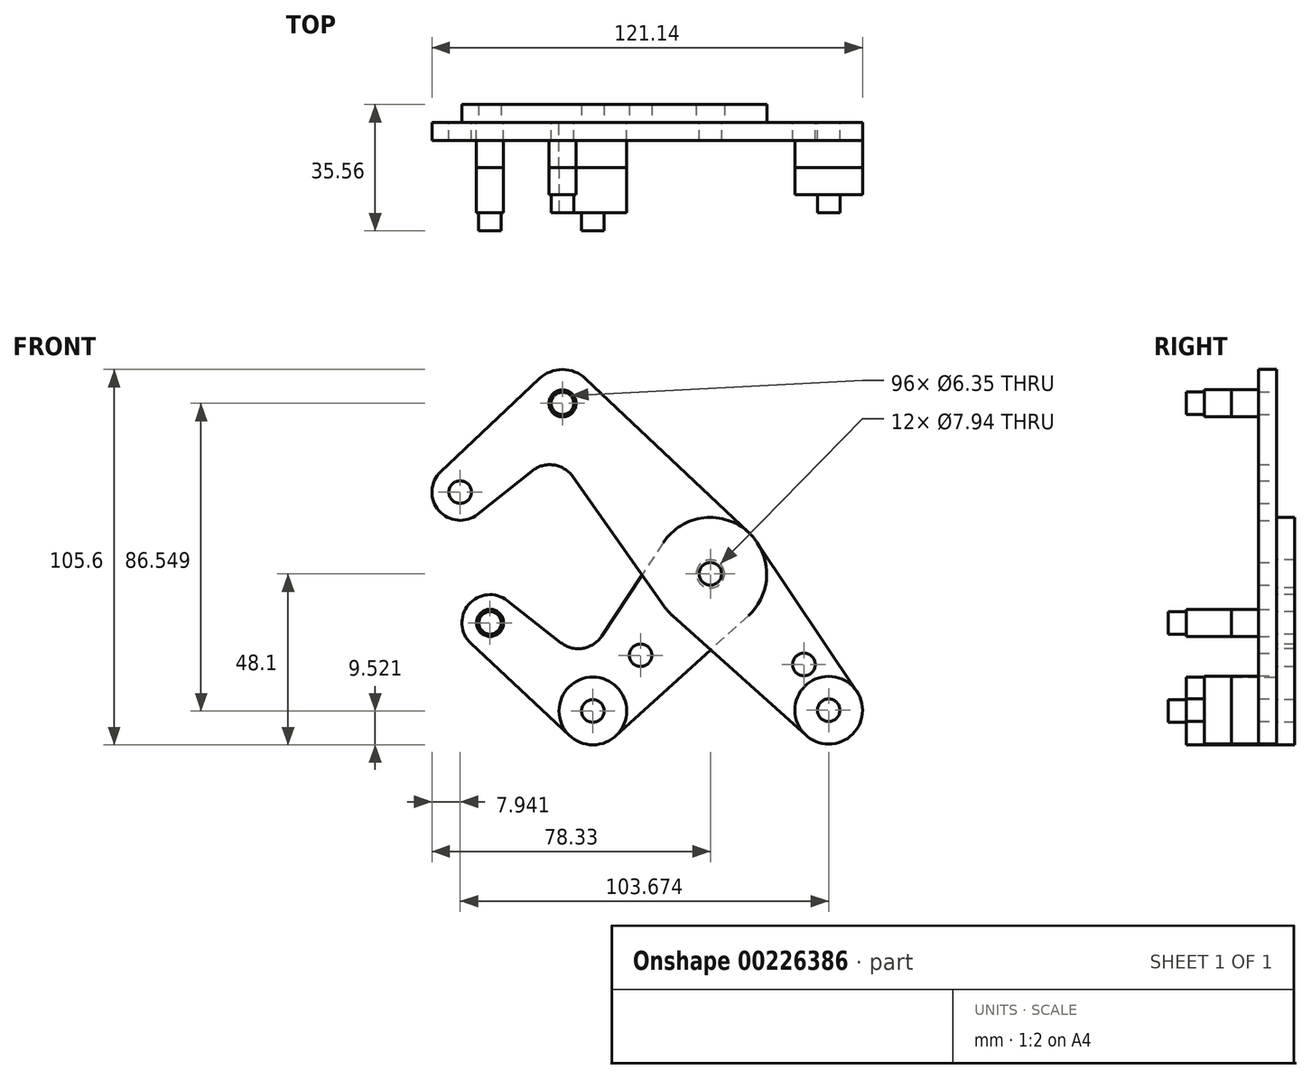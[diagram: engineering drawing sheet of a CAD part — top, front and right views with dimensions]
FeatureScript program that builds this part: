
annotation { "Feature Type Name" : "Feature", "Feature Type Description" : "" }
export const myFeature = defineFeature(function(context is Context, id is Id, definition is map)
    precondition{}
    {
        {
            var Q0;
            Q0=qCreatedBy(makeId("Front.planeOp"),FACE);
            var sketch = newSketch(context, id + "F0", { "sketchPlane" : qUnion([Q0])});
            skLineSegment(sketch, "E0", {"start": v(-41.6, 47.97) * mm, "end": v(41.6, -47.97) * mm, "construction": true});
            skCircle(sketch, "E1", {"center": v(0, 0) * mm, "radius": 3.18 * mm});
            skCircle(sketch, "E2", {"center": v(33.29, -38.38) * mm, "radius": 3.18 * mm});
            skCircle(sketch, "E3", {"center": v(-41.6, 47.97) * mm, "radius": 3.18 * mm});
            skCircle(sketch, "E4", {"center": v(-70.39, 23) * mm, "radius": 3.18 * mm});
            skLineSegment(sketch, "E5", {"start": v(-41.6, 47.97) * mm, "end": v(-70.39, 23) * mm, "construction": true});
            skCircle(sketch, "E6", {"center": v(33.29, -38.38) * mm, "radius": 9.53 * mm});
            skCircle(sketch, "E7", {"center": v(-70.39, 23) * mm, "radius": 7.94 * mm});
            skCircle(sketch, "E8", {"center": v(-41.6, 47.97) * mm, "radius": 9.53 * mm});
            skLineSegment(sketch, "E9", {"start": v(-75.83, 28.78) * mm, "end": v(-48.14, 54.9) * mm});
            skLineSegment(sketch, "E10", {"start": v(-65.44, 16.8) * mm, "end": v(-50.15, 28.98) * mm});
            skCircle(sketch, "E11", {"center": v(0, 0) * mm, "radius": 15.88 * mm});
            skLineSegment(sketch, "E12", {"start": v(-35.07, 54.9) * mm, "end": v(10.9, 11.55) * mm});
            skLineSegment(sketch, "E13", {"start": v(-38.72, 27.35) * mm, "end": v(-12.97, -9.15) * mm});
            skLineSegment(sketch, "E14", {"start": v(-10.6, -11.82) * mm, "end": v(26.93, -45.47) * mm});
            skLineSegment(sketch, "E15", {"start": v(13.2, 8.82) * mm, "end": v(41.2, -33.08) * mm});
            skArc(sketch, "E16.filletArc", {"start": v(-38.72, 27.35) * mm, "mid": v(-44.08, 30.63) * mm, "end": v(-50.15, 28.98) * mm});
            skLineSegment(sketch, "E17", {"start": v(0, 0) * mm, "end": v(-33.05, -38.58) * mm, "construction": true});
            skLineSegment(sketch, "E18", {"start": v(-33.05, -38.58) * mm, "end": v(-61.98, -13.8) * mm, "construction": true});
            skCircle(sketch, "E19", {"center": v(-61.98, -13.8) * mm, "radius": 3.18 * mm});
            skCircle(sketch, "E20", {"center": v(-33.05, -38.58) * mm, "radius": 3.18 * mm});
            skCircle(sketch, "E21", {"center": v(-61.98, -13.8) * mm, "radius": 7.94 * mm});
            skCircle(sketch, "E22", {"center": v(-33.05, -38.58) * mm, "radius": 9.53 * mm});
            skLineSegment(sketch, "E23", {"start": v(-57.08, -7.55) * mm, "end": v(-42.08, -19.35) * mm});
            skLineSegment(sketch, "E24", {"start": v(-67.4, -19.6) * mm, "end": v(-39.54, -45.55) * mm});
            skLineSegment(sketch, "E25", {"start": v(-13.25, 8.74) * mm, "end": v(-30.55, -17.48) * mm});
            skLineSegment(sketch, "E26", {"start": v(10.67, -11.75) * mm, "end": v(-26.65, -45.63) * mm});
            skArc(sketch, "E27.filletArc", {"start": v(-42.08, -19.35) * mm, "mid": v(-35.9, -20.95) * mm, "end": v(-30.55, -17.48) * mm});
            skCircle(sketch, "E28", {"center": v(-19.62, -22.9) * mm, "radius": 3.18 * mm});
            skCircle(sketch, "E29", {"center": v(26.32, -25.5) * mm, "radius": 3.18 * mm});
            skLineSegment(sketch, "E30", {"start": v(26.32, -25.5) * mm, "end": v(23.92, -27.58) * mm, "construction": true});
            skCircle(sketch, "E31", {"center": v(0, 0) * mm, "radius": 3.97 * mm});
            skSolve(sketch);
        }
        {
            var Q0;
            Q0=qCreatedBy(makeId("Front.planeOp"),FACE);
            cPlane(context, id + "F1", {"entities" : qUnion([Q0]), "cplaneType" : CPlaneType.OFFSET, "offset" : 12.7 * mm, "width" : 254 * mm, "height" : 254 * mm});
        }
        {
            var Q0;
            Q0=makeQuery(id+"F0.imprint","IMPRINT",FACE,{"disambiguationData":[TD([[makeQuery(id+"F0.imprint","IMPRINT",EDGE,{"derivedFrom":sQuery(id+"F0.wireOp",EDGE,"E4")}),-1.0]])]});
            var Q1;
            {var subQ1=sQuery(id+"F0.wireOp",EDGE,"E9");Q1=makeQuery(id+"F0.imprint","IMPRINT",FACE,{"disambiguationData":[TD([[makeQuery(id+"F0.imprint","IMPRINT",EDGE,{"derivedFrom":subQ1}),-1.0]])]});}
            var Q2;
            Q2=makeQuery(id+"F0.imprint","IMPRINT",FACE,{"disambiguationData":[TD([[makeQuery(id+"F0.imprint","IMPRINT",EDGE,{"derivedFrom":sQuery(id+"F0.wireOp",EDGE,"E3")}),-1.0]])]});
            var Q3;
            Q3=makeQuery(id+"F0.imprint","IMPRINT",FACE,{"disambiguationData":[TD([[makeQuery(id+"F0.imprint","IMPRINT",EDGE,{"derivedFrom":sQuery(id+"F0.wireOp",EDGE,"E31")}),-1.0]])]});
            var Q4;
            {var subQ0=sQuery(id+"F0.wireOp",EDGE,"E13");var subQ1=sQuery(id+"F0.wireOp",EDGE,"E11");var subQ2=makeQuery(id+"F0.imprint","INTERSECT",VERTEX,{"derivedFrom":[subQ1,subQ0]});Q4=makeQuery(id+"F0.imprint","IMPRINT",FACE,{"disambiguationData":[TD([[makeQuery(id+"F0.imprint","IMPRINT",EDGE,{"disambiguationData":[TD([[subQ2,1.0]])],"derivedFrom":subQ1}),-1.0]])]});}
            var Q5;
            {var subQ0=sQuery(id+"F0.wireOp",EDGE,"E14");var subQ1=sQuery(id+"F0.wireOp",EDGE,"E11");var subQ2=makeQuery(id+"F0.imprint","INTERSECT",VERTEX,{"derivedFrom":[subQ1,subQ0]});Q5=makeQuery(id+"F0.imprint","IMPRINT",FACE,{"disambiguationData":[TD([[makeQuery(id+"F0.imprint","IMPRINT",EDGE,{"disambiguationData":[TD([[subQ2,-1.0]])],"derivedFrom":subQ1}),-1.0]])]});}
            var Q6;
            {var subQ0=sQuery(id+"F0.wireOp",EDGE,"E15");Q6=makeQuery(id+"F0.imprint","IMPRINT",FACE,{"disambiguationData":[TD([[makeQuery(id+"F0.imprint","IMPRINT",EDGE,{"derivedFrom":subQ0}),-1.0]])]});}
            var Q7;
            Q7=makeQuery(id+"F0.imprint","IMPRINT",FACE,{"disambiguationData":[TD([[makeQuery(id+"F0.imprint","IMPRINT",EDGE,{"derivedFrom":sQuery(id+"F0.wireOp",EDGE,"E2")}),-1.0]])]});
            var Q8;
            Q8=makeQuery(id+"F0.imprint","IMPRINT",FACE,{"disambiguationData":[TD([[makeQuery(id+"F0.imprint","IMPRINT",EDGE,{"derivedFrom":sQuery(id+"F0.wireOp",EDGE,"E1")}),-1.0]])]});
            extrude(context, id + "F2", {"entities" : qUnion([Q0, Q1, Q2, Q3, Q4, Q5, Q6, Q7, Q8]), "depth" : 5.08 * mm});
        }
        {
            var Q0;
            Q0=makeQuery(id+"F0.imprint","IMPRINT",FACE,{"disambiguationData":[TD([[makeQuery(id+"F0.imprint","IMPRINT",EDGE,{"derivedFrom":sQuery(id+"F0.wireOp",EDGE,"E31")}),-1.0]])]});
            var Q1;
            {var subQ0=sQuery(id+"F0.wireOp",EDGE,"E14");var subQ1=sQuery(id+"F0.wireOp",EDGE,"E11");var subQ2=makeQuery(id+"F0.imprint","INTERSECT",VERTEX,{"derivedFrom":[subQ1,subQ0]});Q1=makeQuery(id+"F0.imprint","IMPRINT",FACE,{"disambiguationData":[TD([[makeQuery(id+"F0.imprint","IMPRINT",EDGE,{"disambiguationData":[TD([[subQ2,-1.0]])],"derivedFrom":subQ1}),-1.0]])]});}
            var Q2;
            {var subQ10=sQuery(id+"F0.wireOp",EDGE,"E23");Q2=makeQuery(id+"F0.imprint","IMPRINT",FACE,{"disambiguationData":[TD([[makeQuery(id+"F0.imprint","IMPRINT",EDGE,{"derivedFrom":subQ10}),-1.0]])]});}
            var Q3;
            {var subQ0=sQuery(id+"F0.wireOp",EDGE,"E13");var subQ1=sQuery(id+"F0.wireOp",EDGE,"E11");var subQ2=makeQuery(id+"F0.imprint","INTERSECT",VERTEX,{"derivedFrom":[subQ1,subQ0]});Q3=makeQuery(id+"F0.imprint","IMPRINT",FACE,{"disambiguationData":[TD([[makeQuery(id+"F0.imprint","IMPRINT",EDGE,{"disambiguationData":[TD([[subQ2,1.0]])],"derivedFrom":subQ1}),-1.0]])]});}
            var Q4;
            Q4=makeQuery(id+"F0.imprint","IMPRINT",FACE,{"disambiguationData":[TD([[makeQuery(id+"F0.imprint","IMPRINT",EDGE,{"derivedFrom":sQuery(id+"F0.wireOp",EDGE,"E19")}),-1.0]])]});
            var Q5;
            Q5=makeQuery(id+"F0.imprint","IMPRINT",FACE,{"disambiguationData":[TD([[makeQuery(id+"F0.imprint","IMPRINT",EDGE,{"derivedFrom":sQuery(id+"F0.wireOp",EDGE,"E20")}),-1.0]])]});
            extrude(context, id + "F3", {"entities" : qUnion([Q0, Q1, Q2, Q3, Q4, Q5]), "oppositeDirection" : true, "depth" : 5.08 * mm});
        }
        {
            var Q0;
            Q0=makeQuery(id+"F2.opExtrude","CAP_FACE",FACE,{"disambiguationData":[OSD([sQuery(id+"F0.wireOp",EDGE,"E1"),sQuery(id+"F0.wireOp",EDGE,"E2"),sQuery(id+"F0.wireOp",EDGE,"E3"),sQuery(id+"F0.wireOp",EDGE,"E4"),sQuery(id+"F0.wireOp",EDGE,"E6"),sQuery(id+"F0.wireOp",EDGE,"E7"),sQuery(id+"F0.wireOp",EDGE,"E8"),sQuery(id+"F0.wireOp",EDGE,"E9"),sQuery(id+"F0.wireOp",EDGE,"E10"),sQuery(id+"F0.wireOp",EDGE,"E11"),sQuery(id+"F0.wireOp",EDGE,"E12"),sQuery(id+"F0.wireOp",EDGE,"E13"),sQuery(id+"F0.wireOp",EDGE,"E14"),sQuery(id+"F0.wireOp",EDGE,"E15"),sQuery(id+"F0.wireOp",EDGE,"E16.filletArc"),sQuery(id+"F0.wireOp",EDGE,"E29")])],"isStart":true});
            var sketch = newSketch(context, id + "F4", { "sketchPlane" : qUnion([Q0])});
            skCircle(sketch, "E32", {"center": v(41.6, 47.97) * mm, "radius": 3.81 * mm});
            skCircle(sketch, "E33.0", {"center": v(-33.29, -38.38) * mm, "radius": 9.53 * mm});
            skSolve(sketch);
        }
        {
            var Q0;
            Q0=makeQuery(id+"F3.opExtrude","CAP_FACE",FACE,{"disambiguationData":[OSD([sQuery(id+"F0.wireOp",EDGE,"E11"),sQuery(id+"F0.wireOp",EDGE,"E19"),sQuery(id+"F0.wireOp",EDGE,"E20"),sQuery(id+"F0.wireOp",EDGE,"E21"),sQuery(id+"F0.wireOp",EDGE,"E22"),sQuery(id+"F0.wireOp",EDGE,"E23"),sQuery(id+"F0.wireOp",EDGE,"E24"),sQuery(id+"F0.wireOp",EDGE,"E25"),sQuery(id+"F0.wireOp",EDGE,"E26"),sQuery(id+"F0.wireOp",EDGE,"E27.filletArc"),sQuery(id+"F0.wireOp",EDGE,"E28"),sQuery(id+"F0.wireOp",EDGE,"E31")])],"isStart":false});
            var sketch = newSketch(context, id + "F5", { "sketchPlane" : qUnion([Q0])});
            skCircle(sketch, "E34", {"center": v(61.98, -13.8) * mm, "radius": 3.81 * mm});
            skCircle(sketch, "E35.0", {"center": v(33.05, -38.58) * mm, "radius": 9.53 * mm});
            skSolve(sketch);
        }
        {
            var Q0;
            Q0=qSketchRegion(id+"F4",true);
            var Q1;
            Q1=qSketchRegion(id+"F5",true);
            var Q2;
            Q2=qCreatedBy(id+"F1.planeOp",FACE);
            extrude(context, id + "F6", {"entities" : qUnion([Q0, Q1]), "endBound" : BoundingType.UP_TO_SURFACE, "oppositeDirection" : true, "endBoundEntityFace" : qUnion([Q2]), "depth" : 25.4 * mm});
        }
        {
            var Q0;
            Q0=makeQuery(id+"F2.opExtrude","SWEPT_BODY",BODY,{"disambiguationData":[OSD([sQuery(id+"F0.wireOp",EDGE,"E1"),sQuery(id+"F0.wireOp",EDGE,"E2"),sQuery(id+"F0.wireOp",EDGE,"E3"),sQuery(id+"F0.wireOp",EDGE,"E4"),sQuery(id+"F0.wireOp",EDGE,"E6"),sQuery(id+"F0.wireOp",EDGE,"E7"),sQuery(id+"F0.wireOp",EDGE,"E8"),sQuery(id+"F0.wireOp",EDGE,"E9"),sQuery(id+"F0.wireOp",EDGE,"E10"),sQuery(id+"F0.wireOp",EDGE,"E11"),sQuery(id+"F0.wireOp",EDGE,"E12"),sQuery(id+"F0.wireOp",EDGE,"E13"),sQuery(id+"F0.wireOp",EDGE,"E14"),sQuery(id+"F0.wireOp",EDGE,"E15"),sQuery(id+"F0.wireOp",EDGE,"E16.filletArc"),sQuery(id+"F0.wireOp",EDGE,"E29")])]});
            var Q1;
            Q1=makeQuery(id+"F3.opExtrude","SWEPT_BODY",BODY,{"disambiguationData":[OSD([sQuery(id+"F0.wireOp",EDGE,"E11"),sQuery(id+"F0.wireOp",EDGE,"E19"),sQuery(id+"F0.wireOp",EDGE,"E20"),sQuery(id+"F0.wireOp",EDGE,"E21"),sQuery(id+"F0.wireOp",EDGE,"E22"),sQuery(id+"F0.wireOp",EDGE,"E23"),sQuery(id+"F0.wireOp",EDGE,"E24"),sQuery(id+"F0.wireOp",EDGE,"E25"),sQuery(id+"F0.wireOp",EDGE,"E26"),sQuery(id+"F0.wireOp",EDGE,"E27.filletArc"),sQuery(id+"F0.wireOp",EDGE,"E28"),sQuery(id+"F0.wireOp",EDGE,"E31")])]});
            var Q2;
            Q2=makeQuery(id+"F6.opExtrude","SWEPT_BODY",BODY,{"disambiguationData":[OSD([sQuery(id+"F5.wireOp",EDGE,"E34")])]});
            var Q3;
            Q3=makeQuery(id+"F6.opExtrude","SWEPT_BODY",BODY,{"disambiguationData":[OSD([sQuery(id+"F4.wireOp",EDGE,"E32")])]});
            var Q4;
            Q4=makeQuery(id+"F6.opExtrude","SWEPT_BODY",BODY,{"disambiguationData":[OSD([sQuery(id+"F5.wireOp",EDGE,"E35.0")])]});
            var Q5;
            Q5=makeQuery(id+"F6.opExtrude","SWEPT_BODY",BODY,{"disambiguationData":[OSD([sQuery(id+"F4.wireOp",EDGE,"E33.0")])]});
            booleanBodies(context, id + "F7", {"operationType" : BooleanOperationType.SUBTRACTION, "tools" : qUnion([Q0, Q1]), "targets" : qUnion([Q2, Q3, Q4, Q5]), "keepTools" : true});
        }
        {
            var Q0;
            Q0=makeQuery(id+"F6.opExtrude","SWEPT_BODY",BODY,{"disambiguationData":[OSD([sQuery(id+"F4.wireOp",EDGE,"E32")])]});
            var Q1;
            Q1=makeQuery(id+"F6.opExtrude","SWEPT_BODY",BODY,{"disambiguationData":[OSD([sQuery(id+"F4.wireOp",EDGE,"E33.0")])]});
            var Q2;
            Q2=makeQuery(id+"F6.opExtrude","SWEPT_BODY",BODY,{"disambiguationData":[OSD([sQuery(id+"F5.wireOp",EDGE,"E34")])]});
            var Q3;
            Q3=makeQuery(id+"F6.opExtrude","SWEPT_BODY",BODY,{"disambiguationData":[OSD([sQuery(id+"F5.wireOp",EDGE,"E35.0")])]});
            var Q4;
            Q4=qCreatedBy(id+"F1.planeOp",FACE);
            mirror(context, id + "F8", {"entities" : qUnion([Q0, Q1, Q2, Q3]), "mirrorPlane" : qUnion([Q4])});
        }
    });
